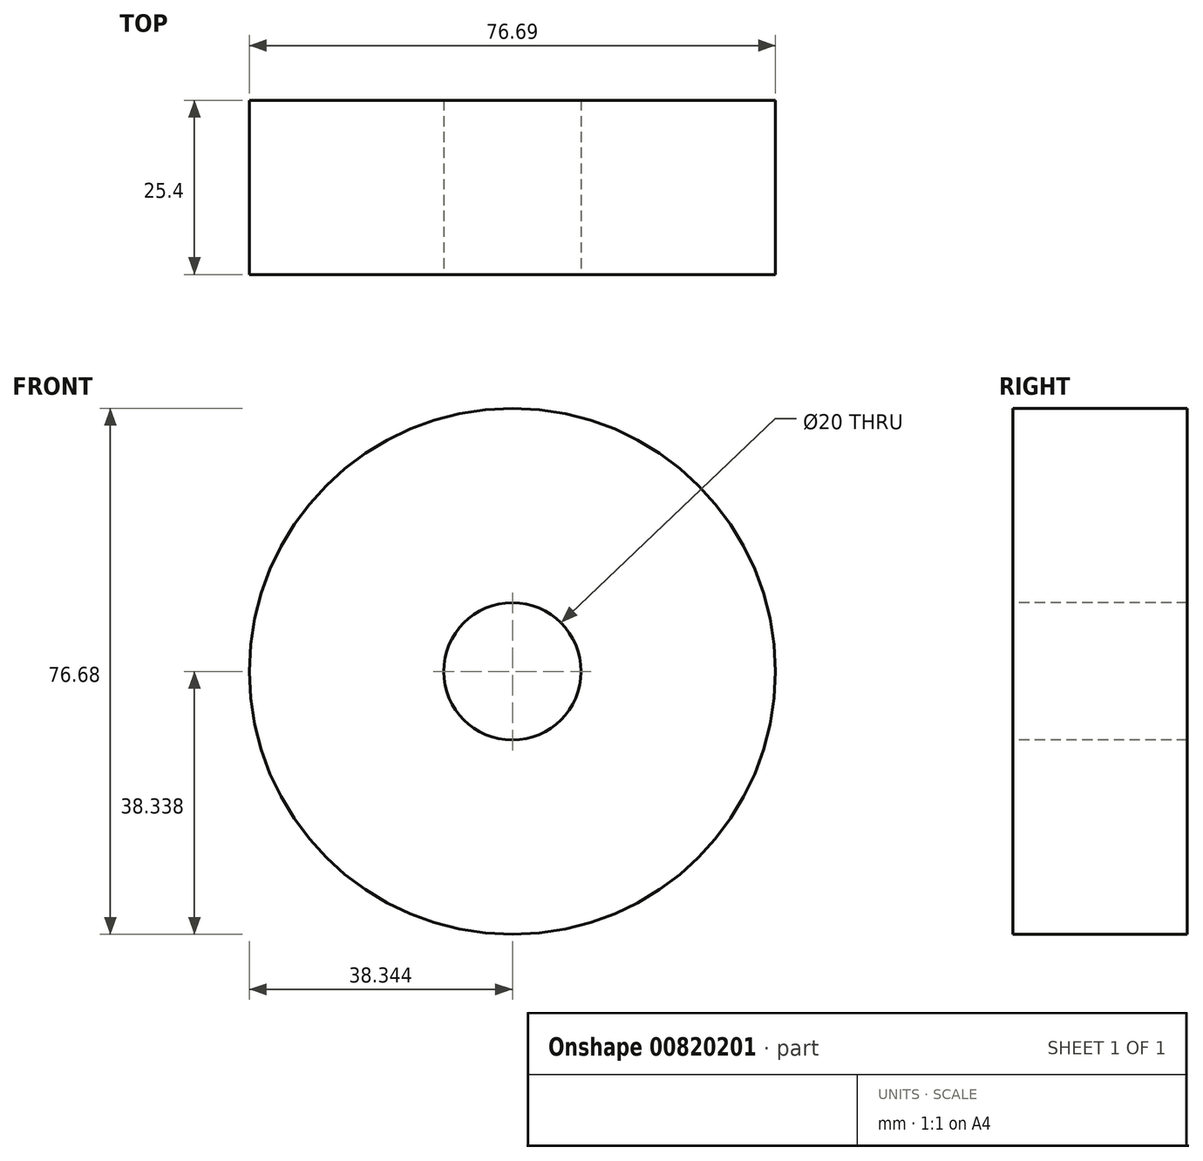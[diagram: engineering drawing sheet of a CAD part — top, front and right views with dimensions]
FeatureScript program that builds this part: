
annotation { "Feature Type Name" : "Feature", "Feature Type Description" : "" }
export const myFeature = defineFeature(function(context is Context, id is Id, definition is map)
    precondition{}
    {
        {
            var Q0;
            Q0=qCreatedBy(makeId("Front.planeOp"),FACE);
            var sketch = newSketch(context, id + "F0", { "sketchPlane" : qUnion([Q0])});
            skCircle(sketch, "E0", {"center": v(10.1, 7.06) * mm, "radius": 38.34 * mm});
            skSolve(sketch);
        }
        {
            var Q0;
            Q0=makeQuery(id+"F0.imprint","IMPRINT",FACE,{"disambiguationData":[TD([[makeQuery(id+"F0.imprint","IMPRINT",EDGE,{"derivedFrom":sQuery(id+"F0.wireOp",EDGE,"E0")}),1.0]])]});
            extrude(context, id + "F1", {"entities" : qUnion([Q0]), "depth" : 25.4 * mm, "offsetDistance" : 25.4 * mm});
        }
        {
            var Q0;
            Q0=makeQuery(id+"F1.opExtrude","CAP_FACE",FACE,{"disambiguationData":[OSD([sQuery(id+"F0.wireOp",EDGE,"E0")])],"isStart":false});
            var sketch = newSketch(context, id + "F2", { "sketchPlane" : qUnion([Q0])});
            skPoint(sketch, "E1", {"position": v(10.1, 7.06) * mm});
            skSolve(sketch);
        }
        {
            var Q0;
            Q0=sQuery(id+"F2.wireOp",VERTEX,"E1");
            var Q1;
            Q1=makeQuery(id+"F1.opExtrude","SWEPT_BODY",BODY,{"disambiguationData":[OSD([sQuery(id+"F0.wireOp",EDGE,"E0")])]});
            hole(context, id + "F3", {"style" : HoleStyle.SIMPLE, "endStyle" : HoleEndStyle.THROUGH, "standardTappedOrClearance" : lookupTablePath({ "standard" : "ISO", "size" : "20", "type" : "Drilled" }), "standardBlindInLast" : lookupTablePath({ "standard" : "ISO", "size" : "20", "type" : "Drilled" }), "holeDiameter" : 20 * mm, "majorDiameter" : 6.35 * mm, "isTappedThrough" : true, "tappedDepth" : 12.7 * mm, "tapClearance" : 3, "locations" : qUnion([Q0]), "scope" : qUnion([Q1])});
        }
    });
